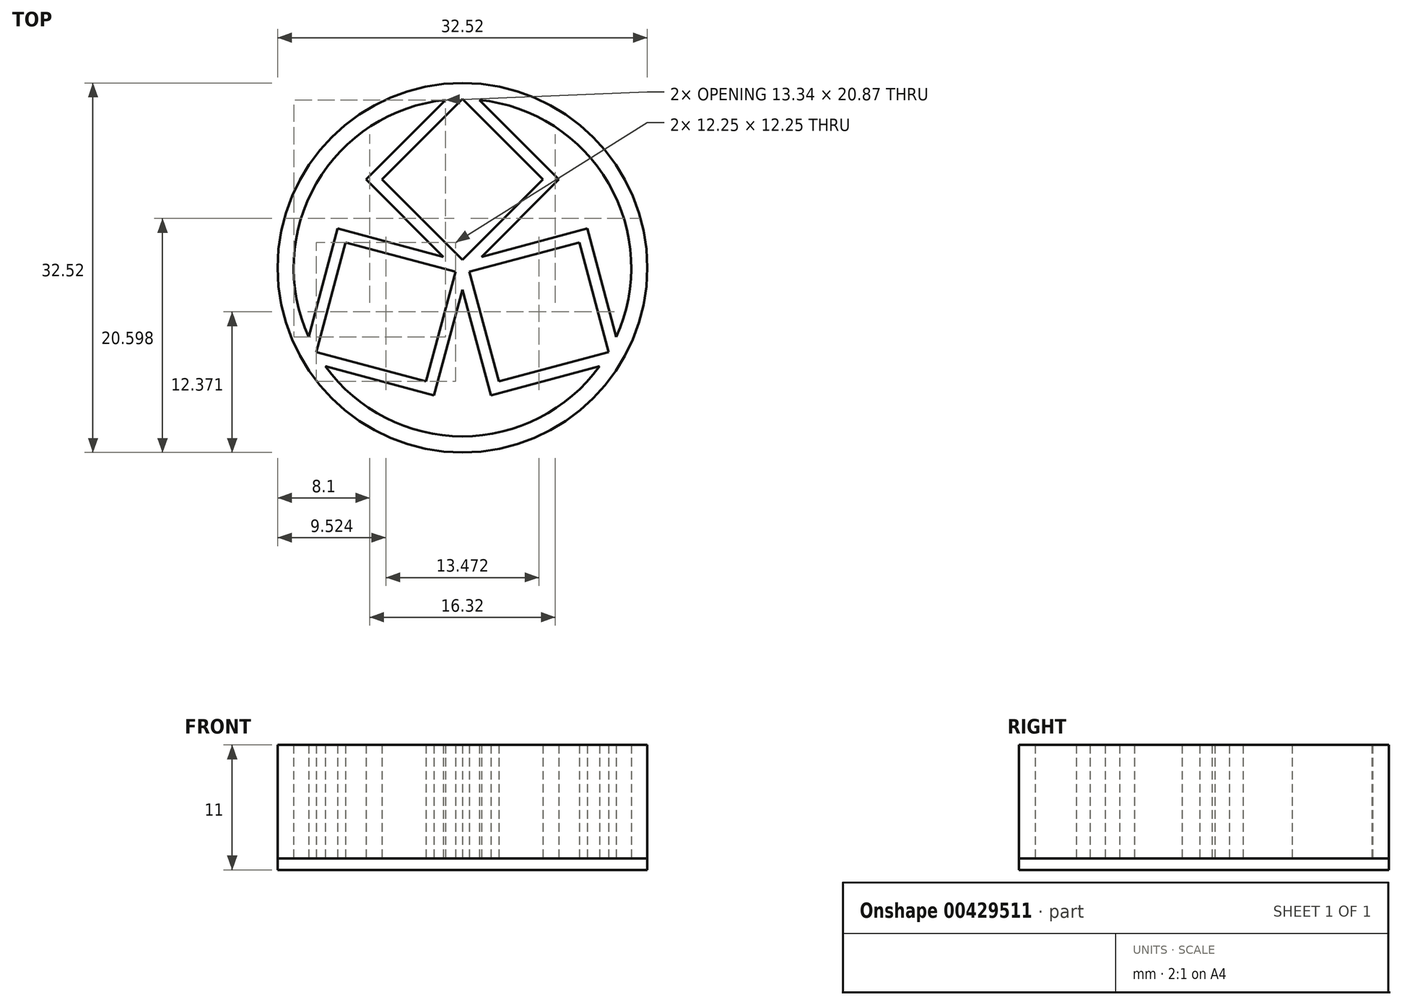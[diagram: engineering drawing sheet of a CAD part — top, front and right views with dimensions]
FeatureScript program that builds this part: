
annotation { "Feature Type Name" : "Feature", "Feature Type Description" : "" }
export const myFeature = defineFeature(function(context is Context, id is Id, definition is map)
    precondition{}
    {
        {
            var Q0;
            Q0=qCreatedBy(makeId("Top.planeOp"),FACE);
            var sketch = newSketch(context, id + "F0", { "sketchPlane" : qUnion([Q0])});
            skLineSegment(sketch, "E0", {"start": v(0, 14.85) * mm, "end": v(7.07, 7.78) * mm});
            skLineSegment(sketch, "E1", {"start": v(0, 14.85) * mm, "end": v(-7.07, 7.78) * mm});
            skLineSegment(sketch, "E2", {"start": v(-7.07, 7.78) * mm, "end": v(0, 0.7) * mm});
            skLineSegment(sketch, "E3", {"start": v(0, 0.7) * mm, "end": v(7.07, 7.78) * mm});
            skLineSegment(sketch, "E4.0", {"start": v(0, -0.7) * mm, "end": v(8.49, 7.78) * mm});
            skLineSegment(sketch, "E4.1", {"start": v(-8.49, 7.78) * mm, "end": v(0, -0.7) * mm});
            skLineSegment(sketch, "E4.2", {"start": v(0, 16.26) * mm, "end": v(-8.49, 7.78) * mm});
            skLineSegment(sketch, "E4.3", {"start": v(0, 16.26) * mm, "end": v(8.49, 7.78) * mm});
            skLineSegment(sketch, "E5", {"start": v(0, 0.7) * mm, "end": v(0, -0.7) * mm, "construction": true});
            skLineSegment(sketch, "E6.1.0", {"start": v(-12.86, -7.42) * mm, "end": v(-3.2, -10.01) * mm});
            skLineSegment(sketch, "E6.1.1", {"start": v(-12.86, -7.42) * mm, "end": v(-10.27, 2.23) * mm});
            skLineSegment(sketch, "E6.1.2", {"start": v(-0.61, -0.35) * mm, "end": v(-10.27, 2.23) * mm});
            skLineSegment(sketch, "E6.1.3", {"start": v(-3.2, -10.01) * mm, "end": v(-0.61, -0.35) * mm});
            skLineSegment(sketch, "E6.1.4", {"start": v(-2.5, -11.24) * mm, "end": v(0.61, 0.35) * mm});
            skLineSegment(sketch, "E6.1.5", {"start": v(-14.08, -8.13) * mm, "end": v(-2.5, -11.24) * mm});
            skLineSegment(sketch, "E6.1.6", {"start": v(-14.08, -8.13) * mm, "end": v(-10.98, 3.46) * mm});
            skLineSegment(sketch, "E6.1.7", {"start": v(0.61, 0.35) * mm, "end": v(-10.98, 3.46) * mm});
            skLineSegment(sketch, "E6.2.0", {"start": v(12.86, -7.42) * mm, "end": v(10.27, 2.23) * mm});
            skLineSegment(sketch, "E6.2.1", {"start": v(12.86, -7.42) * mm, "end": v(3.2, -10.01) * mm});
            skLineSegment(sketch, "E6.2.2", {"start": v(0.61, -0.35) * mm, "end": v(3.2, -10.01) * mm});
            skLineSegment(sketch, "E6.2.3", {"start": v(10.27, 2.23) * mm, "end": v(0.61, -0.35) * mm});
            skLineSegment(sketch, "E6.2.4", {"start": v(10.98, 3.46) * mm, "end": v(-0.61, 0.35) * mm});
            skLineSegment(sketch, "E6.2.5", {"start": v(14.08, -8.13) * mm, "end": v(10.98, 3.46) * mm});
            skLineSegment(sketch, "E6.2.6", {"start": v(14.08, -8.13) * mm, "end": v(2.5, -11.24) * mm});
            skLineSegment(sketch, "E6.2.7", {"start": v(-0.61, 0.35) * mm, "end": v(2.5, -11.24) * mm});
            skPoint(sketch, "E6.center", {"position": v(0, 0) * mm});
            skCircle(sketch, "E7", {"center": v(0, 0) * mm, "radius": 16.26 * mm});
            skCircle(sketch, "E8", {"center": v(0, 0) * mm, "radius": 14.85 * mm});
            skSolve(sketch);
        }
        {
            var Q0;
            {var subQ5=sQuery(id+"F0.wireOp",EDGE,"E4.2");var subQ6=sQuery(id+"F0.wireOp",EDGE,"E4.1");var subQ7=makeQuery(id+"F0.imprint","INTERSECT",VERTEX,{"derivedFrom":[subQ6,subQ5]});Q0=makeQuery(id+"F0.imprint","IMPRINT",FACE,{"disambiguationData":[TD([[makeQuery(id+"F0.imprint","IMPRINT",EDGE,{"disambiguationData":[TD([[subQ7,-1.0]])],"derivedFrom":subQ6}),-1.0]])]});}
            var Q1;
            {var subQ3=sQuery(id+"F0.wireOp",EDGE,"E4.0");var subQ5=sQuery(id+"F0.wireOp",EDGE,"E4.3");var subQ6=makeQuery(id+"F0.imprint","INTERSECT",VERTEX,{"derivedFrom":[subQ3,subQ5]});Q1=makeQuery(id+"F0.imprint","IMPRINT",FACE,{"disambiguationData":[TD([[makeQuery(id+"F0.imprint","IMPRINT",EDGE,{"disambiguationData":[TD([[subQ6,1.0]])],"derivedFrom":subQ3}),-1.0]])]});}
            var Q2;
            Q2=makeQuery(id+"F0.imprint","IMPRINT",FACE,{"disambiguationData":[TD([[makeQuery(id+"F0.imprint","IMPRINT",EDGE,{"derivedFrom":sQuery(id+"F0.wireOp",EDGE,"E6.1.0")}),1.0]])]});
            var Q3;
            Q3=makeQuery(id+"F0.imprint","IMPRINT",FACE,{"disambiguationData":[TD([[makeQuery(id+"F0.imprint","IMPRINT",EDGE,{"derivedFrom":sQuery(id+"F0.wireOp",EDGE,"E6.2.0")}),1.0]])]});
            var Q4;
            {var subQ1=sQuery(id+"F0.wireOp",EDGE,"E4.2");var subQ3=sQuery(id+"F0.wireOp",EDGE,"E8");var subQ4=makeQuery(id+"F0.imprint","INTERSECT",VERTEX,{"derivedFrom":[subQ1,subQ3]});Q4=makeQuery(id+"F0.imprint","IMPRINT",FACE,{"disambiguationData":[TD([[makeQuery(id+"F0.imprint","IMPRINT",EDGE,{"disambiguationData":[TD([[subQ4,-1.0]])],"derivedFrom":subQ3}),-1.0]])]});}
            var Q5;
            {var subQ1=sQuery(id+"F0.wireOp",EDGE,"E4.3");var subQ3=sQuery(id+"F0.wireOp",EDGE,"E8");var subQ4=makeQuery(id+"F0.imprint","INTERSECT",VERTEX,{"derivedFrom":[subQ1,subQ3]});Q5=makeQuery(id+"F0.imprint","IMPRINT",FACE,{"disambiguationData":[TD([[makeQuery(id+"F0.imprint","IMPRINT",EDGE,{"disambiguationData":[TD([[subQ4,1.0]])],"derivedFrom":subQ3}),-1.0]])]});}
            var Q6;
            {var subQ3=sQuery(id+"F0.wireOp",EDGE,"E6.1.4");var subQ5=sQuery(id+"F0.wireOp",EDGE,"E6.1.5");var subQ6=makeQuery(id+"F0.imprint","INTERSECT",VERTEX,{"derivedFrom":[subQ3,subQ5]});Q6=makeQuery(id+"F0.imprint","IMPRINT",FACE,{"disambiguationData":[TD([[makeQuery(id+"F0.imprint","IMPRINT",EDGE,{"disambiguationData":[TD([[subQ6,-1.0]])],"derivedFrom":subQ3}),-1.0]])]});}
            var Q7;
            {var subQ13=sQuery(id+"F0.wireOp",EDGE,"E6.2.0");Q7=makeQuery(id+"F0.imprint","IMPRINT",FACE,{"disambiguationData":[TD([[makeQuery(id+"F0.imprint","IMPRINT",EDGE,{"derivedFrom":subQ13}),-1.0]])]});}
            var Q8;
            {var subQ1=sQuery(id+"F0.wireOp",EDGE,"E6.1.5");var subQ3=sQuery(id+"F0.wireOp",EDGE,"E8");var subQ4=makeQuery(id+"F0.imprint","INTERSECT",VERTEX,{"derivedFrom":[subQ1,subQ3]});Q8=makeQuery(id+"F0.imprint","IMPRINT",FACE,{"disambiguationData":[TD([[makeQuery(id+"F0.imprint","IMPRINT",EDGE,{"disambiguationData":[TD([[subQ4,-1.0]])],"derivedFrom":subQ3}),-1.0]])]});}
            var Q9;
            Q9=makeQuery(id+"F0.imprint","IMPRINT",FACE,{"disambiguationData":[TD([[makeQuery(id+"F0.imprint","IMPRINT",EDGE,{"derivedFrom":sQuery(id+"F0.wireOp",EDGE,"E0")}),-1.0]])]});
            var Q10;
            {var subQ13=sQuery(id+"F0.wireOp",EDGE,"E0");Q10=makeQuery(id+"F0.imprint","IMPRINT",FACE,{"disambiguationData":[TD([[makeQuery(id+"F0.imprint","IMPRINT",EDGE,{"derivedFrom":subQ13}),1.0]])]});}
            var Q11;
            {var subQ14=sQuery(id+"F0.wireOp",EDGE,"E6.1.0");Q11=makeQuery(id+"F0.imprint","IMPRINT",FACE,{"disambiguationData":[TD([[makeQuery(id+"F0.imprint","IMPRINT",EDGE,{"derivedFrom":subQ14}),-1.0]])]});}
            var Q12;
            {var subQ0=sQuery(id+"F0.wireOp",EDGE,"E4.1");var subQ1=sQuery(id+"F0.wireOp",EDGE,"E4.0");var subQ2=makeQuery(id+"F0.imprint","INTERSECT",VERTEX,{"derivedFrom":[subQ1,subQ0]});Q12=makeQuery(id+"F0.imprint","IMPRINT",FACE,{"disambiguationData":[TD([[makeQuery(id+"F0.imprint","IMPRINT",EDGE,{"disambiguationData":[TD([[subQ2,-1.0]])],"derivedFrom":subQ1}),-1.0]])]});}
            var Q13;
            {var subQ1=sQuery(id+"F0.wireOp",EDGE,"E4.2");var subQ3=sQuery(id+"F0.wireOp",EDGE,"E8");var subQ4=makeQuery(id+"F0.imprint","INTERSECT",VERTEX,{"derivedFrom":[subQ1,subQ3]});Q13=makeQuery(id+"F0.imprint","IMPRINT",FACE,{"disambiguationData":[TD([[makeQuery(id+"F0.imprint","IMPRINT",EDGE,{"disambiguationData":[TD([[subQ4,1.0]])],"derivedFrom":subQ1}),1.0]])]});}
            var Q14;
            {var subQ0=sQuery(id+"F0.wireOp",EDGE,"E6.1.7");var subQ1=sQuery(id+"F0.wireOp",EDGE,"E4.1");var subQ2=makeQuery(id+"F0.imprint","INTERSECT",VERTEX,{"derivedFrom":[subQ1,subQ0]});Q14=makeQuery(id+"F0.imprint","IMPRINT",FACE,{"disambiguationData":[TD([[makeQuery(id+"F0.imprint","IMPRINT",EDGE,{"disambiguationData":[TD([[subQ2,-1.0]])],"derivedFrom":subQ1}),1.0]])]});}
            var Q15;
            {var subQ1=sQuery(id+"F0.wireOp",EDGE,"E6.2.5");var subQ3=sQuery(id+"F0.wireOp",EDGE,"E8");var subQ4=makeQuery(id+"F0.imprint","INTERSECT",VERTEX,{"derivedFrom":[subQ1,subQ3]});Q15=makeQuery(id+"F0.imprint","IMPRINT",FACE,{"disambiguationData":[TD([[makeQuery(id+"F0.imprint","IMPRINT",EDGE,{"disambiguationData":[TD([[subQ4,1.0]])],"derivedFrom":subQ1}),1.0]])]});}
            var Q16;
            {var subQ1=sQuery(id+"F0.wireOp",EDGE,"E6.1.5");var subQ3=sQuery(id+"F0.wireOp",EDGE,"E8");var subQ4=makeQuery(id+"F0.imprint","INTERSECT",VERTEX,{"derivedFrom":[subQ1,subQ3]});Q16=makeQuery(id+"F0.imprint","IMPRINT",FACE,{"disambiguationData":[TD([[makeQuery(id+"F0.imprint","IMPRINT",EDGE,{"disambiguationData":[TD([[subQ4,1.0]])],"derivedFrom":subQ1}),1.0]])]});}
            var Q17;
            {var subQ0=sQuery(id+"F0.wireOp",EDGE,"E6.1.4");var subQ1=sQuery(id+"F0.wireOp",EDGE,"E4.0");var subQ2=makeQuery(id+"F0.imprint","INTERSECT",VERTEX,{"derivedFrom":[subQ1,subQ0]});Q17=makeQuery(id+"F0.imprint","IMPRINT",FACE,{"disambiguationData":[TD([[makeQuery(id+"F0.imprint","IMPRINT",EDGE,{"disambiguationData":[TD([[subQ2,-1.0]])],"derivedFrom":subQ1}),1.0]])]});}
            var Q18;
            {var subQ5=sQuery(id+"F0.wireOp",EDGE,"E4.0");var subQ7=sQuery(id+"F0.wireOp",EDGE,"E4.1");var subQ8=makeQuery(id+"F0.imprint","INTERSECT",VERTEX,{"derivedFrom":[subQ5,subQ7]});Q18=makeQuery(id+"F0.imprint","IMPRINT",FACE,{"disambiguationData":[TD([[makeQuery(id+"F0.imprint","IMPRINT",EDGE,{"disambiguationData":[TD([[subQ8,-1.0]])],"derivedFrom":subQ5}),1.0]])]});}
            extrude(context, id + "F1", {"entities" : qUnion([Q0, Q1, Q2, Q3, Q4, Q5, Q6, Q7, Q8, Q9, Q10, Q11, Q12, Q13, Q14, Q15, Q16, Q17, Q18]), "depth" : -1 * mm});
        }
        {
            var Q0;
            {var subQ13=sQuery(id+"F0.wireOp",EDGE,"E6.2.0");Q0=makeQuery(id+"F0.imprint","IMPRINT",FACE,{"disambiguationData":[TD([[makeQuery(id+"F0.imprint","IMPRINT",EDGE,{"derivedFrom":subQ13}),-1.0]])]});}
            var Q1;
            {var subQ1=sQuery(id+"F0.wireOp",EDGE,"E4.3");var subQ3=sQuery(id+"F0.wireOp",EDGE,"E8");var subQ4=makeQuery(id+"F0.imprint","INTERSECT",VERTEX,{"derivedFrom":[subQ1,subQ3]});Q1=makeQuery(id+"F0.imprint","IMPRINT",FACE,{"disambiguationData":[TD([[makeQuery(id+"F0.imprint","IMPRINT",EDGE,{"disambiguationData":[TD([[subQ4,1.0]])],"derivedFrom":subQ3}),-1.0]])]});}
            var Q2;
            {var subQ1=sQuery(id+"F0.wireOp",EDGE,"E4.2");var subQ3=sQuery(id+"F0.wireOp",EDGE,"E8");var subQ4=makeQuery(id+"F0.imprint","INTERSECT",VERTEX,{"derivedFrom":[subQ1,subQ3]});Q2=makeQuery(id+"F0.imprint","IMPRINT",FACE,{"disambiguationData":[TD([[makeQuery(id+"F0.imprint","IMPRINT",EDGE,{"disambiguationData":[TD([[subQ4,-1.0]])],"derivedFrom":subQ3}),-1.0]])]});}
            var Q3;
            {var subQ13=sQuery(id+"F0.wireOp",EDGE,"E0");Q3=makeQuery(id+"F0.imprint","IMPRINT",FACE,{"disambiguationData":[TD([[makeQuery(id+"F0.imprint","IMPRINT",EDGE,{"derivedFrom":subQ13}),1.0]])]});}
            var Q4;
            {var subQ1=sQuery(id+"F0.wireOp",EDGE,"E6.1.5");var subQ3=sQuery(id+"F0.wireOp",EDGE,"E8");var subQ4=makeQuery(id+"F0.imprint","INTERSECT",VERTEX,{"derivedFrom":[subQ1,subQ3]});Q4=makeQuery(id+"F0.imprint","IMPRINT",FACE,{"disambiguationData":[TD([[makeQuery(id+"F0.imprint","IMPRINT",EDGE,{"disambiguationData":[TD([[subQ4,-1.0]])],"derivedFrom":subQ3}),-1.0]])]});}
            var Q5;
            {var subQ14=sQuery(id+"F0.wireOp",EDGE,"E6.1.0");Q5=makeQuery(id+"F0.imprint","IMPRINT",FACE,{"disambiguationData":[TD([[makeQuery(id+"F0.imprint","IMPRINT",EDGE,{"derivedFrom":subQ14}),-1.0]])]});}
            var Q6;
            {var subQ0=sQuery(id+"F0.wireOp",EDGE,"E4.1");var subQ1=sQuery(id+"F0.wireOp",EDGE,"E4.0");var subQ2=makeQuery(id+"F0.imprint","INTERSECT",VERTEX,{"derivedFrom":[subQ1,subQ0]});Q6=makeQuery(id+"F0.imprint","IMPRINT",FACE,{"disambiguationData":[TD([[makeQuery(id+"F0.imprint","IMPRINT",EDGE,{"disambiguationData":[TD([[subQ2,-1.0]])],"derivedFrom":subQ1}),-1.0]])]});}
            var Q7;
            {var subQ1=sQuery(id+"F0.wireOp",EDGE,"E4.2");var subQ3=sQuery(id+"F0.wireOp",EDGE,"E8");var subQ4=makeQuery(id+"F0.imprint","INTERSECT",VERTEX,{"derivedFrom":[subQ1,subQ3]});Q7=makeQuery(id+"F0.imprint","IMPRINT",FACE,{"disambiguationData":[TD([[makeQuery(id+"F0.imprint","IMPRINT",EDGE,{"disambiguationData":[TD([[subQ4,1.0]])],"derivedFrom":subQ1}),1.0]])]});}
            var Q8;
            {var subQ0=sQuery(id+"F0.wireOp",EDGE,"E6.1.7");var subQ1=sQuery(id+"F0.wireOp",EDGE,"E4.1");var subQ2=makeQuery(id+"F0.imprint","INTERSECT",VERTEX,{"derivedFrom":[subQ1,subQ0]});Q8=makeQuery(id+"F0.imprint","IMPRINT",FACE,{"disambiguationData":[TD([[makeQuery(id+"F0.imprint","IMPRINT",EDGE,{"disambiguationData":[TD([[subQ2,-1.0]])],"derivedFrom":subQ1}),1.0]])]});}
            var Q9;
            {var subQ1=sQuery(id+"F0.wireOp",EDGE,"E6.1.5");var subQ3=sQuery(id+"F0.wireOp",EDGE,"E8");var subQ4=makeQuery(id+"F0.imprint","INTERSECT",VERTEX,{"derivedFrom":[subQ1,subQ3]});Q9=makeQuery(id+"F0.imprint","IMPRINT",FACE,{"disambiguationData":[TD([[makeQuery(id+"F0.imprint","IMPRINT",EDGE,{"disambiguationData":[TD([[subQ4,1.0]])],"derivedFrom":subQ1}),1.0]])]});}
            var Q10;
            {var subQ1=sQuery(id+"F0.wireOp",EDGE,"E6.2.5");var subQ3=sQuery(id+"F0.wireOp",EDGE,"E8");var subQ4=makeQuery(id+"F0.imprint","INTERSECT",VERTEX,{"derivedFrom":[subQ1,subQ3]});Q10=makeQuery(id+"F0.imprint","IMPRINT",FACE,{"disambiguationData":[TD([[makeQuery(id+"F0.imprint","IMPRINT",EDGE,{"disambiguationData":[TD([[subQ4,1.0]])],"derivedFrom":subQ1}),1.0]])]});}
            var Q11;
            {var subQ0=sQuery(id+"F0.wireOp",EDGE,"E6.1.4");var subQ1=sQuery(id+"F0.wireOp",EDGE,"E4.0");var subQ2=makeQuery(id+"F0.imprint","INTERSECT",VERTEX,{"derivedFrom":[subQ1,subQ0]});Q11=makeQuery(id+"F0.imprint","IMPRINT",FACE,{"disambiguationData":[TD([[makeQuery(id+"F0.imprint","IMPRINT",EDGE,{"disambiguationData":[TD([[subQ2,-1.0]])],"derivedFrom":subQ1}),1.0]])]});}
            var Q12;
            {var subQ5=sQuery(id+"F0.wireOp",EDGE,"E4.0");var subQ7=sQuery(id+"F0.wireOp",EDGE,"E4.1");var subQ8=makeQuery(id+"F0.imprint","INTERSECT",VERTEX,{"derivedFrom":[subQ5,subQ7]});Q12=makeQuery(id+"F0.imprint","IMPRINT",FACE,{"disambiguationData":[TD([[makeQuery(id+"F0.imprint","IMPRINT",EDGE,{"disambiguationData":[TD([[subQ8,-1.0]])],"derivedFrom":subQ5}),1.0]])]});}
            extrude(context, id + "F2", {"entities" : qUnion([Q0, Q1, Q2, Q3, Q4, Q5, Q6, Q7, Q8, Q9, Q10, Q11, Q12]), "depth" : 10 * mm});
        }
    });
